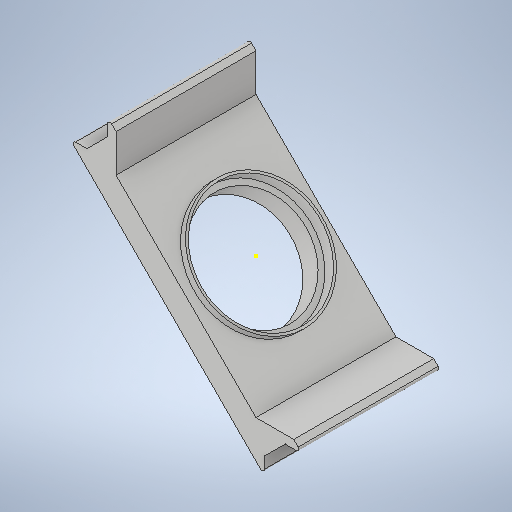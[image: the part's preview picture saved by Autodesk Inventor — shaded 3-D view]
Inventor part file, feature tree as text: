
AUTODESK INVENTOR PART (.ipt)
format: ipt  version: 2025.1 (Build 291241000, 241)  size: 308,736 bytes
history: native  units: mm
features: sketch x7, fillet x4, extrude x2, hole x2
ambient origin geometry x8: Origin, YZ Plane, XZ Plane, XY Plane, X Axis, Y Axis, Z Axis, Center Point
bodies: 实体1 (feature_tree)
feature tree (15):
  extrude  "拉伸1"  Depth=0.5mm
  hole  "孔1"  [1 undecoded]
  sketch  "草图3"  dims[d18=0.5mm d19=25.4mm]
  sketch  "草图4"  dims[d20=1.5mm d21=0.0mm]
  extrude  "拉伸2"  Depth=0.5mm
  hole  "孔2"  [1 undecoded]
  fillet  "圆角1"  Radius=0.5mm
  fillet  "圆角2"  [1 undecoded]
  fillet  "圆角3"  [1 undecoded]
  fillet  "圆角4"  [1 undecoded]
  sketch  "草图7"
  sketch  "草图1"  dims[d6=15.0mm d7=15.0mm d8=0.0mm d9=0.0mm]
  sketch  "草图2"  dims[d10=23.0mm d11=6.0mm d12=25.4mm d13=1.1mm d14=90.0deg d15=0.5mm d16=20.594885mm]
  sketch  "草图5"  dims[d22=25.4mm d23=6.0mm d24=4.0mm d25=2.0mm d26=90.0deg d27=8.0mm d28=20.594885mm d29=0.5mm]
  sketch  "草图6"  dims[d30=0.5mm d31=0.5mm d32=0.5mm d33=0.0mm]
note: 5 required parameter values undecoded (feature->parameter linkage not recoverable at this tier; creation-order binding heuristic only, values carry confidence <= 0.55)
